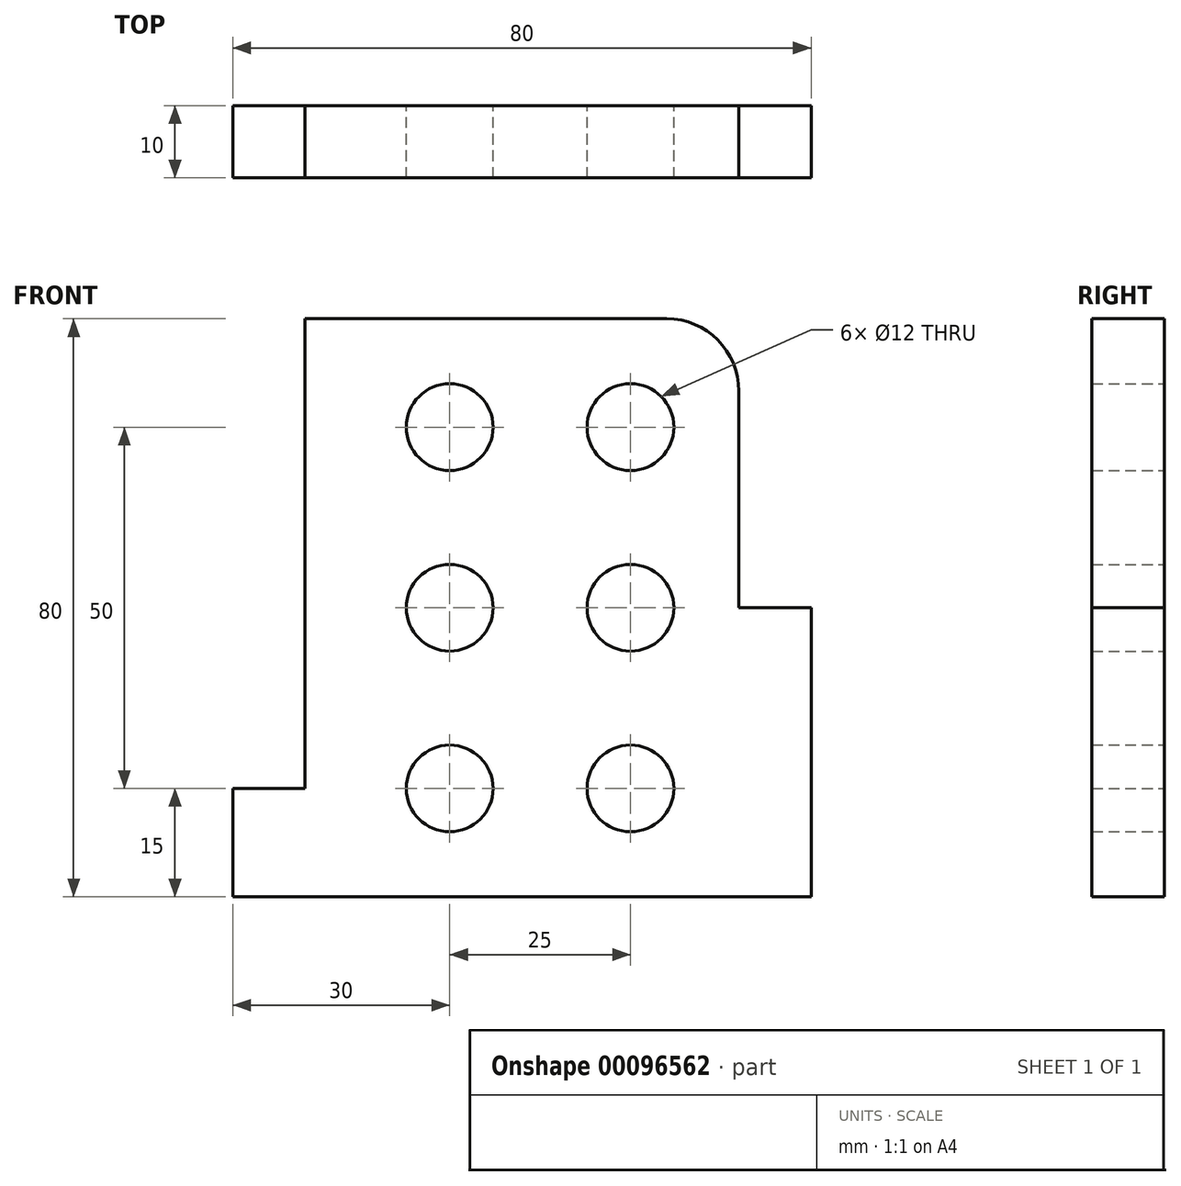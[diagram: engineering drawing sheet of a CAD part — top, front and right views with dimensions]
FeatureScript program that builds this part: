
annotation { "Feature Type Name" : "Feature", "Feature Type Description" : "" }
export const myFeature = defineFeature(function(context is Context, id is Id, definition is map)
    precondition{}
    {
        {
            var Q0;
            Q0=qCreatedBy(makeId("Front.planeOp"),FACE);
            var sketch = newSketch(context, id + "F0", { "sketchPlane" : qUnion([Q0])});
            skLineSegment(sketch, "E0", {"start": v(0, 0) * mm, "end": v(0, 15) * mm});
            skLineSegment(sketch, "E1", {"start": v(0, 15) * mm, "end": v(10, 15) * mm});
            skLineSegment(sketch, "E2", {"start": v(10, 15) * mm, "end": v(10, 80) * mm});
            skLineSegment(sketch, "E3", {"start": v(10, 80) * mm, "end": v(60, 80) * mm});
            skArc(sketch, "E4", {"start": v(70, 70) * mm, "mid": v(67.07, 77.07) * mm, "end": v(60, 80) * mm});
            skLineSegment(sketch, "E5", {"start": v(70, 70) * mm, "end": v(70, 40) * mm});
            skLineSegment(sketch, "E6", {"start": v(70, 40) * mm, "end": v(80, 40) * mm});
            skLineSegment(sketch, "E7", {"start": v(80, 40) * mm, "end": v(80, 0) * mm});
            skLineSegment(sketch, "E8", {"start": v(80, 0) * mm, "end": v(0, 0) * mm});
            skCircle(sketch, "E9", {"center": v(30, 40) * mm, "radius": 6 * mm});
            skCircle(sketch, "E10", {"center": v(55, 40) * mm, "radius": 6 * mm});
            skCircle(sketch, "E11", {"center": v(30, 15) * mm, "radius": 6 * mm});
            skCircle(sketch, "E12", {"center": v(55, 15) * mm, "radius": 6 * mm});
            skCircle(sketch, "E13", {"center": v(30, 65) * mm, "radius": 6 * mm});
            skCircle(sketch, "E14", {"center": v(55, 65) * mm, "radius": 6 * mm});
            skSolve(sketch);
        }
        {
            var Q0;
            Q0 = qSketchRegion(id + "F0", true);
            extrude(context, id + "F1", {"entities" : qUnion([Q0]), "depth" : 10 * mm});
        }
    });
